# Revit family: VT.215
name_source: partatom
category: Арматура трубопроводов
revit_build: Autodesk Revit 2015 (Build: 20140606_1530(x64)
units: mm (PartAtom-declared; Revit-internal decimal feet)

## types (6) — shared parameters
Группа модели = VT.215
Изготовитель = VALTEC S.R.L.
Описание = Кран шаровый полнопроходной

## per-type parameters (varying)
| type | 1 1/2" | 1 1/4" | 1" | 1/2" | 2" | 3/4" | A | G | Lрез | Lручки | Глубина вхождения | Код по классификатору | Сц |
| 3/4" | Нет | Нет | Нет | Нет | Нет | Да | 62 мм | 20 мм | 12 мм | 90 мм | 9 мм | VT.215.N.05 | 28 мм |
| 1/2" | Нет | Нет | Нет | Да | Нет | Нет | 57 мм | 15 мм | 10 мм | 89 мм | 8 мм | VT.215.N.04 | 23 мм |
| 1" | Нет | Нет | Да | Нет | Нет | Нет | 68 мм | 25 мм | 12 мм | 106 мм | 9 мм | VT.215.N.06 | 32 мм |
| 1 1/4" | Нет | Да | Нет | Нет | Нет | Нет | 90 мм | 32 мм | 15 мм | 122 мм | 12 мм | VT.215.N.07 | 40 мм |
| 1 1/2" | Да | Нет | Нет | Нет | Нет | Нет | 102 мм | 40 мм | 15 мм | 154 мм | 12 мм | VT.215.N.08 | 44 мм |
| 2" | Нет | Нет | Нет | Нет | Да | Нет | 114 мм | 50 мм | 15 мм | 153 мм | 12 мм | VT.215.N.09 | 50 мм |
